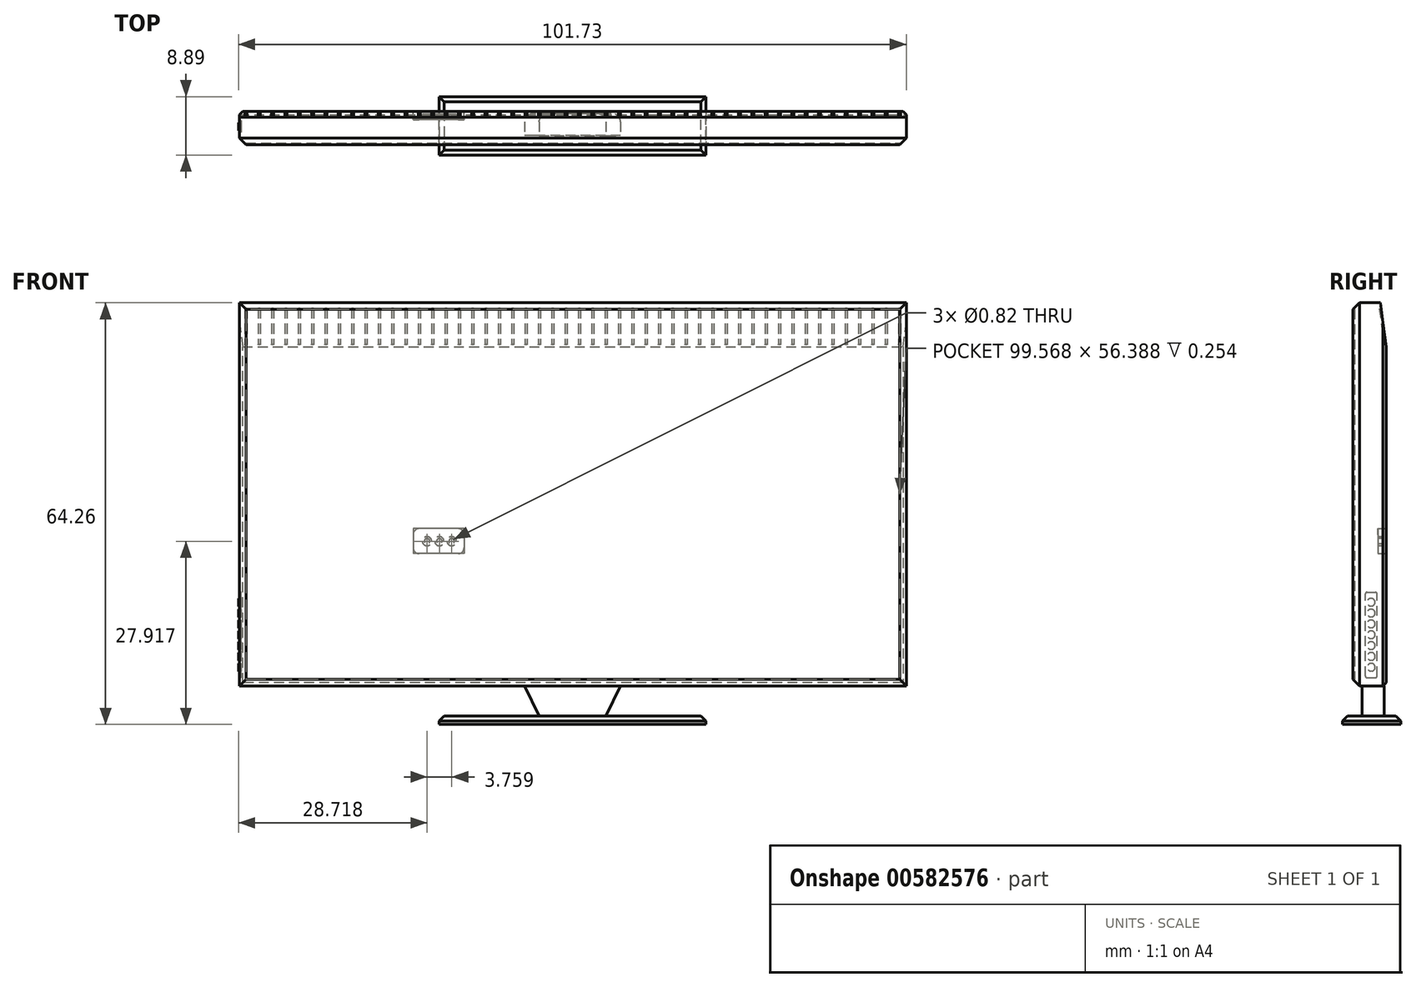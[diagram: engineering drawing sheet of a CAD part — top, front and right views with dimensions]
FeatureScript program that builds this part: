
annotation { "Feature Type Name" : "Feature", "Feature Type Description" : "" }
export const myFeature = defineFeature(function(context is Context, id is Id, definition is map)
    precondition{}
    {
        {
            var Q0;
            Q0=qCreatedBy(makeId("Front.planeOp"),FACE);
            var sketch = newSketch(context, id + "F0", { "sketchPlane" : qUnion([Q0])});
            skLineSegment(sketch, "E0", {"start": v(-47.44, 48.24) * mm, "end": v(54.16, 48.24) * mm});
            skLineSegment(sketch, "E1", {"start": v(54.16, 48.24) * mm, "end": v(54.16, -10.18) * mm});
            skLineSegment(sketch, "E2", {"start": v(54.16, -10.18) * mm, "end": v(-47.44, -10.18) * mm});
            skLineSegment(sketch, "E3", {"start": v(-47.44, -10.18) * mm, "end": v(-47.44, 48.24) * mm});
            skLineSegment(sketch, "E4", {"start": v(3.33, -14.75) * mm, "end": v(8.41, -14.75) * mm});
            skLineSegment(sketch, "E5", {"start": v(8.41, -14.75) * mm, "end": v(10.63, -10.18) * mm});
            skLineSegment(sketch, "E6", {"start": v(3.33, -14.75) * mm, "end": v(-1.75, -14.75) * mm});
            skLineSegment(sketch, "E7", {"start": v(-1.75, -14.75) * mm, "end": v(-3.97, -10.18) * mm});
            skSolve(sketch);
        }
        {
            var Q0;
            Q0=makeQuery(id+"F0.imprint","IMPRINT",FACE,{"disambiguationData":[TD([[makeQuery(id+"F0.imprint","IMPRINT",EDGE,{"derivedFrom":sQuery(id+"F0.wireOp",EDGE,"E0")}),-1.0]])]});
            extrude(context, id + "F1", {"entities" : qUnion([Q0]), "oppositeDirection" : true, "depth" : 5.08 * mm, "offsetDistance" : 25.4 * mm});
        }
        {
            var Q0;
            Q0=makeQuery(id+"F1.opExtrude","CAP_FACE",FACE,{"disambiguationData":[OSD([sQuery(id+"F0.wireOp",EDGE,"E0"),sQuery(id+"F0.wireOp",EDGE,"E1"),sQuery(id+"F0.wireOp",EDGE,"E2"),sQuery(id+"F0.wireOp",EDGE,"E3")])],"isStart":true});
            var sketch = newSketch(context, id + "F2", { "sketchPlane" : qUnion([Q0])});
            skLineSegment(sketch, "E8", {"start": v(-45.63, 49.46) * mm, "end": v(52.17, 49.46) * mm});
            skLineSegment(sketch, "E9", {"start": v(52.17, 49.46) * mm, "end": v(52.17, -7.5) * mm});
            skLineSegment(sketch, "E10", {"start": v(52.17, -7.5) * mm, "end": v(-45.41, -7.5) * mm});
            skLineSegment(sketch, "E11", {"start": v(-45.41, -7.5) * mm, "end": v(-45.63, 49.46) * mm});
            skSolve(sketch);
        }
        {
            var Q0;
            Q0=makeQuery(id+"F2.imprint","IMPRINT",FACE,{"disambiguationData":[TD([[makeQuery(id+"F2.imprint","IMPRINT",EDGE,{"derivedFrom":sQuery(id+"F2.wireOp",EDGE,"E8")}),-1.0]])]});
            extrude(context, id + "F3", {"entities" : qUnion([Q0]), "operationType" : NewBodyOperationType.REMOVE, "oppositeDirection" : true, "depth" : 0.5 * mm, "offsetDistance" : 25.4 * mm});
        }
        {
            var Q0;
            Q0=makeQuery(id+"F1.opExtrude","CAP_EDGE",EDGE,{"disambiguationData":[OSD([sQuery(id+"F0.wireOp",EDGE,"E3")])],"isStart":true});
            chamfer(context, id + "F4", {"entities" : qUnion([Q0]), "width" : 1.02 * mm, "tangentPropagation" : true});
        }
        {
            var Q0;
            Q0=makeQuery(id+"F1.opExtrude","CAP_EDGE",EDGE,{"disambiguationData":[OSD([sQuery(id+"F0.wireOp",EDGE,"E0")])],"isStart":true});
            chamfer(context, id + "F5", {"entities" : qUnion([Q0]), "width" : 1.02 * mm, "tangentPropagation" : true});
        }
        {
            var Q0;
            Q0=makeQuery(id+"F1.opExtrude","CAP_EDGE",EDGE,{"disambiguationData":[OSD([sQuery(id+"F0.wireOp",EDGE,"E1")])],"isStart":true});
            chamfer(context, id + "F6", {"entities" : qUnion([Q0]), "width" : 1.02 * mm, "tangentPropagation" : true});
        }
        {
            var Q0;
            Q0=makeQuery(id+"F1.opExtrude","CAP_EDGE",EDGE,{"disambiguationData":[OSD([sQuery(id+"F0.wireOp",EDGE,"E2")])],"isStart":true});
            chamfer(context, id + "F7", {"entities" : qUnion([Q0]), "width" : 1.02 * mm, "tangentPropagation" : true});
        }
        {
            var Q0;
            Q0=makeQuery(id+"F1.opExtrude","SWEPT_FACE",FACE,{"disambiguationData":[OSD([sQuery(id+"F0.wireOp",EDGE,"E1")])]});
            var sketch = newSketch(context, id + "F8", { "sketchPlane" : qUnion([Q0])});
            skLineSegment(sketch, "E12", {"start": v(4.16, 48.24) * mm, "end": v(5.08, 41.52) * mm});
            skLineSegment(sketch, "E13", {"start": v(5.08, 41.52) * mm, "end": v(5.08, 48.24) * mm});
            skLineSegment(sketch, "E14", {"start": v(5.08, 48.24) * mm, "end": v(4.16, 48.24) * mm});
            skSolve(sketch);
        }
        {
            var Q0;
            Q0=makeQuery(id+"F8.imprint","IMPRINT",FACE,{"disambiguationData":[TD([[makeQuery(id+"F8.imprint","IMPRINT",EDGE,{"derivedFrom":sQuery(id+"F8.wireOp",EDGE,"E12")}),1.0]])]});
            var Q1;
            Q1=makeQuery(id+"F1.opExtrude","SWEPT_FACE",FACE,{"disambiguationData":[OSD([sQuery(id+"F0.wireOp",EDGE,"E3")])]});
            extrude(context, id + "F9", {"entities" : qUnion([Q0]), "operationType" : NewBodyOperationType.REMOVE, "endBound" : BoundingType.UP_TO_SURFACE, "oppositeDirection" : true, "depth" : 25.4 * mm, "endBoundEntityFace" : qUnion([Q1]), "offsetDistance" : 25.4 * mm});
        }
        {
            var Q0;
            Q0=makeQuery(id+"F0.imprint","IMPRINT",FACE,{"disambiguationData":[TD([[makeQuery(id+"F0.imprint","IMPRINT",EDGE,{"derivedFrom":sQuery(id+"F0.wireOp",EDGE,"E4")}),1.0]])]});
            extrude(context, id + "F10", {"entities" : qUnion([Q0]), "oppositeDirection" : true, "depth" : 4.75 * mm, "offsetDistance" : 25.4 * mm});
        }
        {
            var Q0;
            Q0=makeQuery(id+"F10.opExtrude","CAP_FACE",FACE,{"disambiguationData":[OSD([sQuery(id+"F0.wireOp",EDGE,"E2"),sQuery(id+"F0.wireOp",EDGE,"E4"),sQuery(id+"F0.wireOp",EDGE,"E5"),sQuery(id+"F0.wireOp",EDGE,"E6"),sQuery(id+"F0.wireOp",EDGE,"E7")])],"isStart":true});
            extrude(context, id + "F11", {"entities" : qUnion([Q0]), "operationType" : NewBodyOperationType.REMOVE, "oppositeDirection" : true, "depth" : 1.4 * mm, "offsetDistance" : 25.4 * mm});
        }
        {
            var Q0;
            Q0=makeQuery(id+"F10.opExtrude","SWEPT_FACE",FACE,{"disambiguationData":[OSD([sQuery(id+"F0.wireOp",EDGE,"E4"),sQuery(id+"F0.wireOp",EDGE,"E6")])]});
            var sketch = newSketch(context, id + "F12", { "sketchPlane" : qUnion([Q0])});
            skLineSegment(sketch, "E15", {"start": v(3.33, -3.07) * mm, "end": v(3.33, 1.6) * mm});
            skPoint(sketch, "E15.startSnap0", {"position": v(3.33, -1.4) * mm});
            skPoint(sketch, "E15.startSnap1", {"position": v(-1.75, -3.07) * mm});
            skLineSegment(sketch, "E16", {"start": v(3.33, 1.6) * mm, "end": v(3.33, -3.07) * mm});
            skLineSegment(sketch, "E17", {"start": v(3.33, -7.3) * mm, "end": v(3.33, -3.07) * mm});
            skLineSegment(sketch, "E18", {"start": v(-16.99, 1.6) * mm, "end": v(23.65, 1.6) * mm});
            skLineSegment(sketch, "E19", {"start": v(23.65, 1.6) * mm, "end": v(23.65, -7.3) * mm});
            skLineSegment(sketch, "E20", {"start": v(23.65, -7.3) * mm, "end": v(-16.99, -7.3) * mm});
            skLineSegment(sketch, "E21", {"start": v(-16.99, -7.3) * mm, "end": v(-16.99, 1.6) * mm});
            skSolve(sketch);
        }
        {
            var Q0;
            {var subQ3=sQuery(id+"F12.wireOp",EDGE,"E21");Q0=makeQuery(id+"F12.imprint","IMPRINT",FACE,{"disambiguationData":[TD([[makeQuery(id+"F12.imprint","IMPRINT",EDGE,{"derivedFrom":subQ3}),-1.0]])]});}
            var Q1;
            {var subQ0=sQuery(id+"F12.wireOp",EDGE,"E19");Q1=makeQuery(id+"F12.imprint","IMPRINT",FACE,{"disambiguationData":[TD([[makeQuery(id+"F12.imprint","IMPRINT",EDGE,{"derivedFrom":subQ0}),-1.0]])]});}
            var Q2;
            {var subQ0=sQuery(id+"F0.wireOp",EDGE,"E4");var subQ1=makeQuery(id+"F10.opExtrude","SWEPT_EDGE",EDGE,{"disambiguationData":[OSD([subQ0,sQuery(id+"F0.wireOp",EDGE,"E5")])]});Q2=makeQuery(id+"F12.imprint","IMPRINT",FACE,{"disambiguationData":[TD([[makeQuery(id+"F12.imprint","IMPRINT",EDGE,{"derivedFrom":subQ1}),1.0]])]});}
            var Q3;
            {var subQ0=sQuery(id+"F0.wireOp",EDGE,"E6");var subQ1=makeQuery(id+"F10.opExtrude","SWEPT_EDGE",EDGE,{"disambiguationData":[OSD([subQ0,sQuery(id+"F0.wireOp",EDGE,"E7")])]});Q3=makeQuery(id+"F12.imprint","IMPRINT",FACE,{"disambiguationData":[TD([[makeQuery(id+"F12.imprint","IMPRINT",EDGE,{"derivedFrom":subQ1}),-1.0]])]});}
            extrude(context, id + "F13", {"entities" : qUnion([Q0, Q1, Q2, Q3]), "operationType" : NewBodyOperationType.ADD, "depth" : 1.27 * mm, "offsetDistance" : 25.4 * mm});
        }
        {
            var Q0;
            Q0=makeQuery(id+"F10.opExtrude","CAP_EDGE",EDGE,{"disambiguationData":[OSD([sQuery(id+"F0.wireOp",EDGE,"E7")])],"isStart":false});
            var Q1;
            Q1=makeQuery(id+"F11.boolean.opBoolean","COPY",EDGE,{"derivedFrom":makeQuery(id+"F11.opExtrude","CAP_EDGE",EDGE,{"disambiguationData":[OSD([sQuery(id+"F0.wireOp",EDGE,"E7")])],"isStart":false})});
            var Q2;
            Q2=makeQuery(id+"F11.boolean.opBoolean","COPY",EDGE,{"derivedFrom":makeQuery(id+"F11.opExtrude","CAP_EDGE",EDGE,{"disambiguationData":[OSD([sQuery(id+"F0.wireOp",EDGE,"E5")])],"isStart":false})});
            var Q3;
            Q3=makeQuery(id+"F10.opExtrude","CAP_EDGE",EDGE,{"disambiguationData":[OSD([sQuery(id+"F0.wireOp",EDGE,"E5")])],"isStart":false});
            fillet(context, id + "F14", {"entities" : qUnion([Q0, Q1, Q2, Q3]), "radius" : 1.27 * mm, "tangentPropagation" : true, "allowEdgeOverflow" : false});
        }
        {
            var Q0;
            Q0=makeQuery(id+"F13.opExtrude","CAP_EDGE",EDGE,{"disambiguationData":[OSD([sQuery(id+"F12.wireOp",EDGE,"E21")])],"isStart":true});
            var Q1;
            Q1=makeQuery(id+"F13.opExtrude","CAP_EDGE",EDGE,{"disambiguationData":[OSD([sQuery(id+"F12.wireOp",EDGE,"E18")])],"isStart":true});
            var Q2;
            Q2=makeQuery(id+"F13.opExtrude","CAP_EDGE",EDGE,{"disambiguationData":[OSD([sQuery(id+"F12.wireOp",EDGE,"E19")])],"isStart":true});
            var Q3;
            Q3=makeQuery(id+"F13.opExtrude","CAP_EDGE",EDGE,{"disambiguationData":[OSD([sQuery(id+"F12.wireOp",EDGE,"E20")])],"isStart":true});
            chamfer(context, id + "F15", {"entities" : qUnion([Q0, Q1, Q2, Q3]), "width" : 0.76 * mm, "tangentPropagation" : true});
        }
        {
            var Q0;
            Q0=makeQuery(id+"F1.opExtrude","CAP_EDGE",EDGE,{"disambiguationData":[OSD([sQuery(id+"F0.wireOp",EDGE,"E3")])],"isStart":false});
            var Q1;
            Q1=makeQuery(id+"F1.opExtrude","CAP_EDGE",EDGE,{"disambiguationData":[OSD([sQuery(id+"F0.wireOp",EDGE,"E1")])],"isStart":false});
            var Q2;
            Q2=makeQuery(id+"F1.opExtrude","CAP_EDGE",EDGE,{"disambiguationData":[OSD([sQuery(id+"F0.wireOp",EDGE,"E2")])],"isStart":false});
            var Q3;
            Q3=makeQuery(id+"F9.boolean.opBoolean","COPY",EDGE,{"derivedFrom":makeQuery(id+"F9.opExtrude","SWEPT_EDGE",EDGE,{"disambiguationData":[OSD([sQuery(id+"F0.wireOp",EDGE,"E0"),sQuery(id+"F0.wireOp",EDGE,"E1"),sQuery(id+"F8.wireOp",EDGE,"E12"),sQuery(id+"F8.wireOp",EDGE,"E14")])]})});
            chamfer(context, id + "F16", {"entities" : qUnion([Q0, Q1, Q2, Q3]), "width" : 0.5 * mm, "tangentPropagation" : true});
        }
        {
            var Q0;
            Q0=makeQuery(id+"F1.opExtrude","CAP_FACE",FACE,{"disambiguationData":[OSD([sQuery(id+"F0.wireOp",EDGE,"E0"),sQuery(id+"F0.wireOp",EDGE,"E1"),sQuery(id+"F0.wireOp",EDGE,"E2"),sQuery(id+"F0.wireOp",EDGE,"E3")])],"isStart":true});
            extrude(context, id + "F17", {"entities" : qUnion([Q0]), "operationType" : NewBodyOperationType.REMOVE, "oppositeDirection" : true, "depth" : 0.25 * mm, "offsetDistance" : 25.4 * mm});
        }
        {
            var Q0;
            Q0=makeQuery(id+"F17.boolean.opBoolean","COPY",FACE,{"derivedFrom":makeQuery(id+"F17.opExtrude","CAP_FACE",FACE,{"disambiguationData":[OSD([sQuery(id+"F0.wireOp",EDGE,"E0"),sQuery(id+"F0.wireOp",EDGE,"E1"),sQuery(id+"F0.wireOp",EDGE,"E2"),sQuery(id+"F0.wireOp",EDGE,"E3")])],"isStart":false})});
            extrude(context, id + "F18", {"entities" : qUnion([Q0]), "depth" : 0.03 * mm, "offsetDistance" : 25.4 * mm});
        }
        {
            var Q0;
            Q0=makeQuery(id+"F9.boolean.opBoolean","COPY",FACE,{"derivedFrom":makeQuery(id+"F9.opExtrude","SWEPT_FACE",FACE,{"disambiguationData":[OSD([sQuery(id+"F8.wireOp",EDGE,"E12")])]})});
            var sketch = newSketch(context, id + "F19", { "sketchPlane" : qUnion([Q0])});
            skLineSegment(sketch, "E22.bottom", {"start": v(-53.3, 46.33) * mm, "end": v(-53, 46.33) * mm});
            skLineSegment(sketch, "E22.top", {"start": v(-53.3, 40.82) * mm, "end": v(-53, 40.82) * mm});
            skLineSegment(sketch, "E22.left", {"start": v(-53.3, 46.33) * mm, "end": v(-53.3, 40.82) * mm});
            skLineSegment(sketch, "E22.right", {"start": v(-53, 46.33) * mm, "end": v(-53, 40.82) * mm});
            skLineSegment(sketch, "E23.1.0.0", {"start": v(-51.28, 46.33) * mm, "end": v(-51.28, 40.82) * mm});
            skLineSegment(sketch, "E23.1.0.1", {"start": v(-50.96, 46.33) * mm, "end": v(-50.96, 40.82) * mm});
            skLineSegment(sketch, "E23.1.0.2", {"start": v(-51.28, 40.82) * mm, "end": v(-50.96, 40.82) * mm});
            skLineSegment(sketch, "E23.1.0.3", {"start": v(-51.28, 46.33) * mm, "end": v(-50.96, 46.33) * mm});
            skLineSegment(sketch, "E23.2.0.0", {"start": v(-49.24, 46.33) * mm, "end": v(-49.24, 40.82) * mm});
            skLineSegment(sketch, "E23.2.0.1", {"start": v(-48.93, 46.33) * mm, "end": v(-48.93, 40.82) * mm});
            skLineSegment(sketch, "E23.2.0.2", {"start": v(-49.24, 40.82) * mm, "end": v(-48.93, 40.82) * mm});
            skLineSegment(sketch, "E23.2.0.3", {"start": v(-49.24, 46.33) * mm, "end": v(-48.93, 46.33) * mm});
            skLineSegment(sketch, "E23.3.0.0", {"start": v(-47.21, 46.33) * mm, "end": v(-47.21, 40.82) * mm});
            skLineSegment(sketch, "E23.3.0.1", {"start": v(-46.9, 46.33) * mm, "end": v(-46.9, 40.82) * mm});
            skLineSegment(sketch, "E23.3.0.2", {"start": v(-47.21, 40.82) * mm, "end": v(-46.9, 40.82) * mm});
            skLineSegment(sketch, "E23.3.0.3", {"start": v(-47.21, 46.33) * mm, "end": v(-46.9, 46.33) * mm});
            skLineSegment(sketch, "E23.4.0.0", {"start": v(-45.18, 46.33) * mm, "end": v(-45.18, 40.82) * mm});
            skLineSegment(sketch, "E23.4.0.1", {"start": v(-44.86, 46.33) * mm, "end": v(-44.86, 40.82) * mm});
            skLineSegment(sketch, "E23.4.0.2", {"start": v(-45.18, 40.82) * mm, "end": v(-44.86, 40.82) * mm});
            skLineSegment(sketch, "E23.4.0.3", {"start": v(-45.18, 46.33) * mm, "end": v(-44.86, 46.33) * mm});
            skLineSegment(sketch, "E23.5.0.0", {"start": v(-43.15, 46.33) * mm, "end": v(-43.15, 40.82) * mm});
            skLineSegment(sketch, "E23.5.0.1", {"start": v(-42.83, 46.33) * mm, "end": v(-42.83, 40.82) * mm});
            skLineSegment(sketch, "E23.5.0.2", {"start": v(-43.15, 40.82) * mm, "end": v(-42.83, 40.82) * mm});
            skLineSegment(sketch, "E23.5.0.3", {"start": v(-43.15, 46.33) * mm, "end": v(-42.83, 46.33) * mm});
            skLineSegment(sketch, "E23.6.0.0", {"start": v(-41.12, 46.33) * mm, "end": v(-41.12, 40.82) * mm});
            skLineSegment(sketch, "E23.6.0.1", {"start": v(-40.8, 46.33) * mm, "end": v(-40.8, 40.82) * mm});
            skLineSegment(sketch, "E23.6.0.2", {"start": v(-41.12, 40.82) * mm, "end": v(-40.8, 40.82) * mm});
            skLineSegment(sketch, "E23.6.0.3", {"start": v(-41.12, 46.33) * mm, "end": v(-40.8, 46.33) * mm});
            skLineSegment(sketch, "E23.7.0.0", {"start": v(-39.08, 46.33) * mm, "end": v(-39.08, 40.82) * mm});
            skLineSegment(sketch, "E23.7.0.1", {"start": v(-38.77, 46.33) * mm, "end": v(-38.77, 40.82) * mm});
            skLineSegment(sketch, "E23.7.0.2", {"start": v(-39.08, 40.82) * mm, "end": v(-38.77, 40.82) * mm});
            skLineSegment(sketch, "E23.7.0.3", {"start": v(-39.08, 46.33) * mm, "end": v(-38.77, 46.33) * mm});
            skLineSegment(sketch, "E23.8.0.0", {"start": v(-37.05, 46.33) * mm, "end": v(-37.05, 40.82) * mm});
            skLineSegment(sketch, "E23.8.0.1", {"start": v(-36.74, 46.33) * mm, "end": v(-36.74, 40.82) * mm});
            skLineSegment(sketch, "E23.8.0.2", {"start": v(-37.05, 40.82) * mm, "end": v(-36.74, 40.82) * mm});
            skLineSegment(sketch, "E23.8.0.3", {"start": v(-37.05, 46.33) * mm, "end": v(-36.74, 46.33) * mm});
            skLineSegment(sketch, "E23.9.0.0", {"start": v(-35.02, 46.33) * mm, "end": v(-35.02, 40.82) * mm});
            skLineSegment(sketch, "E23.9.0.1", {"start": v(-34.7, 46.33) * mm, "end": v(-34.7, 40.82) * mm});
            skLineSegment(sketch, "E23.9.0.2", {"start": v(-35.02, 40.82) * mm, "end": v(-34.7, 40.82) * mm});
            skLineSegment(sketch, "E23.9.0.3", {"start": v(-35.02, 46.33) * mm, "end": v(-34.7, 46.33) * mm});
            skLineSegment(sketch, "E23.10.0.0", {"start": v(-32.99, 46.33) * mm, "end": v(-32.99, 40.82) * mm});
            skLineSegment(sketch, "E23.10.0.1", {"start": v(-32.67, 46.33) * mm, "end": v(-32.67, 40.82) * mm});
            skLineSegment(sketch, "E23.10.0.2", {"start": v(-32.99, 40.82) * mm, "end": v(-32.67, 40.82) * mm});
            skLineSegment(sketch, "E23.10.0.3", {"start": v(-32.99, 46.33) * mm, "end": v(-32.67, 46.33) * mm});
            skLineSegment(sketch, "E23.11.0.0", {"start": v(-30.96, 46.33) * mm, "end": v(-30.96, 40.82) * mm});
            skLineSegment(sketch, "E23.11.0.1", {"start": v(-30.64, 46.33) * mm, "end": v(-30.64, 40.82) * mm});
            skLineSegment(sketch, "E23.11.0.2", {"start": v(-30.96, 40.82) * mm, "end": v(-30.64, 40.82) * mm});
            skLineSegment(sketch, "E23.11.0.3", {"start": v(-30.96, 46.33) * mm, "end": v(-30.64, 46.33) * mm});
            skLineSegment(sketch, "E23.12.0.0", {"start": v(-28.92, 46.33) * mm, "end": v(-28.92, 40.82) * mm});
            skLineSegment(sketch, "E23.12.0.1", {"start": v(-28.6, 46.33) * mm, "end": v(-28.6, 40.82) * mm});
            skLineSegment(sketch, "E23.12.0.2", {"start": v(-28.92, 40.82) * mm, "end": v(-28.6, 40.82) * mm});
            skLineSegment(sketch, "E23.12.0.3", {"start": v(-28.92, 46.33) * mm, "end": v(-28.6, 46.33) * mm});
            skLineSegment(sketch, "E23.13.0.0", {"start": v(-26.9, 46.33) * mm, "end": v(-26.9, 40.82) * mm});
            skLineSegment(sketch, "E23.13.0.1", {"start": v(-26.58, 46.33) * mm, "end": v(-26.58, 40.82) * mm});
            skLineSegment(sketch, "E23.13.0.2", {"start": v(-26.9, 40.82) * mm, "end": v(-26.58, 40.82) * mm});
            skLineSegment(sketch, "E23.13.0.3", {"start": v(-26.9, 46.33) * mm, "end": v(-26.58, 46.33) * mm});
            skLineSegment(sketch, "E23.14.0.0", {"start": v(-24.86, 46.33) * mm, "end": v(-24.86, 40.82) * mm});
            skLineSegment(sketch, "E23.14.0.1", {"start": v(-24.54, 46.33) * mm, "end": v(-24.54, 40.82) * mm});
            skLineSegment(sketch, "E23.14.0.2", {"start": v(-24.86, 40.82) * mm, "end": v(-24.54, 40.82) * mm});
            skLineSegment(sketch, "E23.14.0.3", {"start": v(-24.86, 46.33) * mm, "end": v(-24.54, 46.33) * mm});
            skLineSegment(sketch, "E23.15.0.0", {"start": v(-22.83, 46.33) * mm, "end": v(-22.83, 40.82) * mm});
            skLineSegment(sketch, "E23.15.0.1", {"start": v(-22.51, 46.33) * mm, "end": v(-22.51, 40.82) * mm});
            skLineSegment(sketch, "E23.15.0.2", {"start": v(-22.83, 40.82) * mm, "end": v(-22.51, 40.82) * mm});
            skLineSegment(sketch, "E23.15.0.3", {"start": v(-22.83, 46.33) * mm, "end": v(-22.51, 46.33) * mm});
            skLineSegment(sketch, "E23.16.0.0", {"start": v(-20.8, 46.33) * mm, "end": v(-20.8, 40.82) * mm});
            skLineSegment(sketch, "E23.16.0.1", {"start": v(-20.48, 46.33) * mm, "end": v(-20.48, 40.82) * mm});
            skLineSegment(sketch, "E23.16.0.2", {"start": v(-20.8, 40.82) * mm, "end": v(-20.48, 40.82) * mm});
            skLineSegment(sketch, "E23.16.0.3", {"start": v(-20.8, 46.33) * mm, "end": v(-20.48, 46.33) * mm});
            skLineSegment(sketch, "E23.17.0.0", {"start": v(-18.76, 46.33) * mm, "end": v(-18.76, 40.82) * mm});
            skLineSegment(sketch, "E23.17.0.1", {"start": v(-18.45, 46.33) * mm, "end": v(-18.45, 40.82) * mm});
            skLineSegment(sketch, "E23.17.0.2", {"start": v(-18.76, 40.82) * mm, "end": v(-18.45, 40.82) * mm});
            skLineSegment(sketch, "E23.17.0.3", {"start": v(-18.76, 46.33) * mm, "end": v(-18.45, 46.33) * mm});
            skLineSegment(sketch, "E23.18.0.0", {"start": v(-16.73, 46.33) * mm, "end": v(-16.73, 40.82) * mm});
            skLineSegment(sketch, "E23.18.0.1", {"start": v(-16.42, 46.33) * mm, "end": v(-16.42, 40.82) * mm});
            skLineSegment(sketch, "E23.18.0.2", {"start": v(-16.73, 40.82) * mm, "end": v(-16.42, 40.82) * mm});
            skLineSegment(sketch, "E23.18.0.3", {"start": v(-16.73, 46.33) * mm, "end": v(-16.42, 46.33) * mm});
            skLineSegment(sketch, "E23.19.0.0", {"start": v(-14.7, 46.33) * mm, "end": v(-14.7, 40.82) * mm});
            skLineSegment(sketch, "E23.19.0.1", {"start": v(-14.38, 46.33) * mm, "end": v(-14.38, 40.82) * mm});
            skLineSegment(sketch, "E23.19.0.2", {"start": v(-14.7, 40.82) * mm, "end": v(-14.38, 40.82) * mm});
            skLineSegment(sketch, "E23.19.0.3", {"start": v(-14.7, 46.33) * mm, "end": v(-14.38, 46.33) * mm});
            skLineSegment(sketch, "E23.20.0.0", {"start": v(-12.67, 46.33) * mm, "end": v(-12.67, 40.82) * mm});
            skLineSegment(sketch, "E23.20.0.1", {"start": v(-12.35, 46.33) * mm, "end": v(-12.35, 40.82) * mm});
            skLineSegment(sketch, "E23.20.0.2", {"start": v(-12.67, 40.82) * mm, "end": v(-12.35, 40.82) * mm});
            skLineSegment(sketch, "E23.20.0.3", {"start": v(-12.67, 46.33) * mm, "end": v(-12.35, 46.33) * mm});
            skLineSegment(sketch, "E23.21.0.0", {"start": v(-10.64, 46.33) * mm, "end": v(-10.64, 40.82) * mm});
            skLineSegment(sketch, "E23.21.0.1", {"start": v(-10.32, 46.33) * mm, "end": v(-10.32, 40.82) * mm});
            skLineSegment(sketch, "E23.21.0.2", {"start": v(-10.64, 40.82) * mm, "end": v(-10.32, 40.82) * mm});
            skLineSegment(sketch, "E23.21.0.3", {"start": v(-10.64, 46.33) * mm, "end": v(-10.32, 46.33) * mm});
            skLineSegment(sketch, "E23.22.0.0", {"start": v(-8.6, 46.33) * mm, "end": v(-8.6, 40.82) * mm});
            skLineSegment(sketch, "E23.22.0.1", {"start": v(-8.29, 46.33) * mm, "end": v(-8.29, 40.82) * mm});
            skLineSegment(sketch, "E23.22.0.2", {"start": v(-8.6, 40.82) * mm, "end": v(-8.29, 40.82) * mm});
            skLineSegment(sketch, "E23.22.0.3", {"start": v(-8.6, 46.33) * mm, "end": v(-8.29, 46.33) * mm});
            skLineSegment(sketch, "E23.23.0.0", {"start": v(-6.57, 46.33) * mm, "end": v(-6.57, 40.82) * mm});
            skLineSegment(sketch, "E23.23.0.1", {"start": v(-6.26, 46.33) * mm, "end": v(-6.26, 40.82) * mm});
            skLineSegment(sketch, "E23.23.0.2", {"start": v(-6.57, 40.82) * mm, "end": v(-6.26, 40.82) * mm});
            skLineSegment(sketch, "E23.23.0.3", {"start": v(-6.57, 46.33) * mm, "end": v(-6.26, 46.33) * mm});
            skLineSegment(sketch, "E23.24.0.0", {"start": v(-4.54, 46.33) * mm, "end": v(-4.54, 40.82) * mm});
            skLineSegment(sketch, "E23.24.0.1", {"start": v(-4.22, 46.33) * mm, "end": v(-4.22, 40.82) * mm});
            skLineSegment(sketch, "E23.24.0.2", {"start": v(-4.54, 40.82) * mm, "end": v(-4.22, 40.82) * mm});
            skLineSegment(sketch, "E23.24.0.3", {"start": v(-4.54, 46.33) * mm, "end": v(-4.22, 46.33) * mm});
            skLineSegment(sketch, "E23.25.0.0", {"start": v(-2.5, 46.33) * mm, "end": v(-2.5, 40.82) * mm});
            skLineSegment(sketch, "E23.25.0.1", {"start": v(-2.2, 46.33) * mm, "end": v(-2.2, 40.82) * mm});
            skLineSegment(sketch, "E23.25.0.2", {"start": v(-2.5, 40.82) * mm, "end": v(-2.2, 40.82) * mm});
            skLineSegment(sketch, "E23.25.0.3", {"start": v(-2.5, 46.33) * mm, "end": v(-2.2, 46.33) * mm});
            skLineSegment(sketch, "E23.26.0.0", {"start": v(-0.48, 46.33) * mm, "end": v(-0.48, 40.82) * mm});
            skLineSegment(sketch, "E23.26.0.1", {"start": v(-0.16, 46.33) * mm, "end": v(-0.16, 40.82) * mm});
            skLineSegment(sketch, "E23.26.0.2", {"start": v(-0.48, 40.82) * mm, "end": v(-0.16, 40.82) * mm});
            skLineSegment(sketch, "E23.26.0.3", {"start": v(-0.48, 46.33) * mm, "end": v(-0.16, 46.33) * mm});
            skLineSegment(sketch, "E23.27.0.0", {"start": v(1.56, 46.33) * mm, "end": v(1.56, 40.82) * mm});
            skLineSegment(sketch, "E23.27.0.1", {"start": v(1.87, 46.33) * mm, "end": v(1.87, 40.82) * mm});
            skLineSegment(sketch, "E23.27.0.2", {"start": v(1.56, 40.82) * mm, "end": v(1.87, 40.82) * mm});
            skLineSegment(sketch, "E23.27.0.3", {"start": v(1.56, 46.33) * mm, "end": v(1.87, 46.33) * mm});
            skLineSegment(sketch, "E23.28.0.0", {"start": v(3.59, 46.33) * mm, "end": v(3.59, 40.82) * mm});
            skLineSegment(sketch, "E23.28.0.1", {"start": v(3.9, 46.33) * mm, "end": v(3.9, 40.82) * mm});
            skLineSegment(sketch, "E23.28.0.2", {"start": v(3.59, 40.82) * mm, "end": v(3.9, 40.82) * mm});
            skLineSegment(sketch, "E23.28.0.3", {"start": v(3.59, 46.33) * mm, "end": v(3.9, 46.33) * mm});
            skLineSegment(sketch, "E23.29.0.0", {"start": v(5.62, 46.33) * mm, "end": v(5.62, 40.82) * mm});
            skLineSegment(sketch, "E23.29.0.1", {"start": v(5.94, 46.33) * mm, "end": v(5.94, 40.82) * mm});
            skLineSegment(sketch, "E23.29.0.2", {"start": v(5.62, 40.82) * mm, "end": v(5.94, 40.82) * mm});
            skLineSegment(sketch, "E23.29.0.3", {"start": v(5.62, 46.33) * mm, "end": v(5.94, 46.33) * mm});
            skLineSegment(sketch, "E23.30.0.0", {"start": v(7.65, 46.33) * mm, "end": v(7.65, 40.82) * mm});
            skLineSegment(sketch, "E23.30.0.1", {"start": v(7.97, 46.33) * mm, "end": v(7.97, 40.82) * mm});
            skLineSegment(sketch, "E23.30.0.2", {"start": v(7.65, 40.82) * mm, "end": v(7.97, 40.82) * mm});
            skLineSegment(sketch, "E23.30.0.3", {"start": v(7.65, 46.33) * mm, "end": v(7.97, 46.33) * mm});
            skLineSegment(sketch, "E23.31.0.0", {"start": v(9.68, 46.33) * mm, "end": v(9.68, 40.82) * mm});
            skLineSegment(sketch, "E23.31.0.1", {"start": v(10, 46.33) * mm, "end": v(10, 40.82) * mm});
            skLineSegment(sketch, "E23.31.0.2", {"start": v(9.68, 40.82) * mm, "end": v(10, 40.82) * mm});
            skLineSegment(sketch, "E23.31.0.3", {"start": v(9.68, 46.33) * mm, "end": v(10, 46.33) * mm});
            skLineSegment(sketch, "E23.32.0.0", {"start": v(11.72, 46.33) * mm, "end": v(11.72, 40.82) * mm});
            skLineSegment(sketch, "E23.32.0.1", {"start": v(12.03, 46.33) * mm, "end": v(12.03, 40.82) * mm});
            skLineSegment(sketch, "E23.32.0.2", {"start": v(11.72, 40.82) * mm, "end": v(12.03, 40.82) * mm});
            skLineSegment(sketch, "E23.32.0.3", {"start": v(11.72, 46.33) * mm, "end": v(12.03, 46.33) * mm});
            skLineSegment(sketch, "E23.33.0.0", {"start": v(13.75, 46.33) * mm, "end": v(13.75, 40.82) * mm});
            skLineSegment(sketch, "E23.33.0.1", {"start": v(14.06, 46.33) * mm, "end": v(14.06, 40.82) * mm});
            skLineSegment(sketch, "E23.33.0.2", {"start": v(13.75, 40.82) * mm, "end": v(14.06, 40.82) * mm});
            skLineSegment(sketch, "E23.33.0.3", {"start": v(13.75, 46.33) * mm, "end": v(14.06, 46.33) * mm});
            skLineSegment(sketch, "E23.34.0.0", {"start": v(15.78, 46.33) * mm, "end": v(15.78, 40.82) * mm});
            skLineSegment(sketch, "E23.34.0.1", {"start": v(16.1, 46.33) * mm, "end": v(16.1, 40.82) * mm});
            skLineSegment(sketch, "E23.34.0.2", {"start": v(15.78, 40.82) * mm, "end": v(16.1, 40.82) * mm});
            skLineSegment(sketch, "E23.34.0.3", {"start": v(15.78, 46.33) * mm, "end": v(16.1, 46.33) * mm});
            skLineSegment(sketch, "E23.35.0.0", {"start": v(17.81, 46.33) * mm, "end": v(17.81, 40.82) * mm});
            skLineSegment(sketch, "E23.35.0.1", {"start": v(18.13, 46.33) * mm, "end": v(18.13, 40.82) * mm});
            skLineSegment(sketch, "E23.35.0.2", {"start": v(17.81, 40.82) * mm, "end": v(18.13, 40.82) * mm});
            skLineSegment(sketch, "E23.35.0.3", {"start": v(17.81, 46.33) * mm, "end": v(18.13, 46.33) * mm});
            skLineSegment(sketch, "E23.36.0.0", {"start": v(19.84, 46.33) * mm, "end": v(19.84, 40.82) * mm});
            skLineSegment(sketch, "E23.36.0.1", {"start": v(20.16, 46.33) * mm, "end": v(20.16, 40.82) * mm});
            skLineSegment(sketch, "E23.36.0.2", {"start": v(19.84, 40.82) * mm, "end": v(20.16, 40.82) * mm});
            skLineSegment(sketch, "E23.36.0.3", {"start": v(19.84, 46.33) * mm, "end": v(20.16, 46.33) * mm});
            skLineSegment(sketch, "E23.37.0.0", {"start": v(21.88, 46.33) * mm, "end": v(21.88, 40.82) * mm});
            skLineSegment(sketch, "E23.37.0.1", {"start": v(22.2, 46.33) * mm, "end": v(22.2, 40.82) * mm});
            skLineSegment(sketch, "E23.37.0.2", {"start": v(21.88, 40.82) * mm, "end": v(22.2, 40.82) * mm});
            skLineSegment(sketch, "E23.37.0.3", {"start": v(21.88, 46.33) * mm, "end": v(22.2, 46.33) * mm});
            skLineSegment(sketch, "E23.38.0.0", {"start": v(23.9, 46.33) * mm, "end": v(23.9, 40.82) * mm});
            skLineSegment(sketch, "E23.38.0.1", {"start": v(24.22, 46.33) * mm, "end": v(24.22, 40.82) * mm});
            skLineSegment(sketch, "E23.38.0.2", {"start": v(23.9, 40.82) * mm, "end": v(24.22, 40.82) * mm});
            skLineSegment(sketch, "E23.38.0.3", {"start": v(23.9, 46.33) * mm, "end": v(24.22, 46.33) * mm});
            skLineSegment(sketch, "E23.39.0.0", {"start": v(25.94, 46.33) * mm, "end": v(25.94, 40.82) * mm});
            skLineSegment(sketch, "E23.39.0.1", {"start": v(26.26, 46.33) * mm, "end": v(26.26, 40.82) * mm});
            skLineSegment(sketch, "E23.39.0.2", {"start": v(25.94, 40.82) * mm, "end": v(26.26, 40.82) * mm});
            skLineSegment(sketch, "E23.39.0.3", {"start": v(25.94, 46.33) * mm, "end": v(26.26, 46.33) * mm});
            skLineSegment(sketch, "E23.40.0.0", {"start": v(27.97, 46.33) * mm, "end": v(27.97, 40.82) * mm});
            skLineSegment(sketch, "E23.40.0.1", {"start": v(28.29, 46.33) * mm, "end": v(28.29, 40.82) * mm});
            skLineSegment(sketch, "E23.40.0.2", {"start": v(27.97, 40.82) * mm, "end": v(28.29, 40.82) * mm});
            skLineSegment(sketch, "E23.40.0.3", {"start": v(27.97, 46.33) * mm, "end": v(28.29, 46.33) * mm});
            skLineSegment(sketch, "E23.41.0.0", {"start": v(30, 46.33) * mm, "end": v(30, 40.82) * mm});
            skLineSegment(sketch, "E23.41.0.1", {"start": v(30.32, 46.33) * mm, "end": v(30.32, 40.82) * mm});
            skLineSegment(sketch, "E23.41.0.2", {"start": v(30, 40.82) * mm, "end": v(30.32, 40.82) * mm});
            skLineSegment(sketch, "E23.41.0.3", {"start": v(30, 46.33) * mm, "end": v(30.32, 46.33) * mm});
            skLineSegment(sketch, "E23.42.0.0", {"start": v(32.04, 46.33) * mm, "end": v(32.04, 40.82) * mm});
            skLineSegment(sketch, "E23.42.0.1", {"start": v(32.35, 46.33) * mm, "end": v(32.35, 40.82) * mm});
            skLineSegment(sketch, "E23.42.0.2", {"start": v(32.04, 40.82) * mm, "end": v(32.35, 40.82) * mm});
            skLineSegment(sketch, "E23.42.0.3", {"start": v(32.04, 46.33) * mm, "end": v(32.35, 46.33) * mm});
            skLineSegment(sketch, "E23.43.0.0", {"start": v(34.07, 46.33) * mm, "end": v(34.07, 40.82) * mm});
            skLineSegment(sketch, "E23.43.0.1", {"start": v(34.38, 46.33) * mm, "end": v(34.38, 40.82) * mm});
            skLineSegment(sketch, "E23.43.0.2", {"start": v(34.07, 40.82) * mm, "end": v(34.38, 40.82) * mm});
            skLineSegment(sketch, "E23.43.0.3", {"start": v(34.07, 46.33) * mm, "end": v(34.38, 46.33) * mm});
            skLineSegment(sketch, "E23.44.0.0", {"start": v(36.1, 46.33) * mm, "end": v(36.1, 40.82) * mm});
            skLineSegment(sketch, "E23.44.0.1", {"start": v(36.42, 46.33) * mm, "end": v(36.42, 40.82) * mm});
            skLineSegment(sketch, "E23.44.0.2", {"start": v(36.1, 40.82) * mm, "end": v(36.42, 40.82) * mm});
            skLineSegment(sketch, "E23.44.0.3", {"start": v(36.1, 46.33) * mm, "end": v(36.42, 46.33) * mm});
            skLineSegment(sketch, "E23.45.0.0", {"start": v(38.13, 46.33) * mm, "end": v(38.13, 40.82) * mm});
            skLineSegment(sketch, "E23.45.0.1", {"start": v(38.45, 46.33) * mm, "end": v(38.45, 40.82) * mm});
            skLineSegment(sketch, "E23.45.0.2", {"start": v(38.13, 40.82) * mm, "end": v(38.45, 40.82) * mm});
            skLineSegment(sketch, "E23.45.0.3", {"start": v(38.13, 46.33) * mm, "end": v(38.45, 46.33) * mm});
            skLineSegment(sketch, "E23.46.0.0", {"start": v(40.16, 46.33) * mm, "end": v(40.16, 40.82) * mm});
            skLineSegment(sketch, "E23.46.0.1", {"start": v(40.48, 46.33) * mm, "end": v(40.48, 40.82) * mm});
            skLineSegment(sketch, "E23.46.0.2", {"start": v(40.16, 40.82) * mm, "end": v(40.48, 40.82) * mm});
            skLineSegment(sketch, "E23.46.0.3", {"start": v(40.16, 46.33) * mm, "end": v(40.48, 46.33) * mm});
            skLineSegment(sketch, "E23.47.0.0", {"start": v(42.2, 46.33) * mm, "end": v(42.2, 40.82) * mm});
            skLineSegment(sketch, "E23.47.0.1", {"start": v(42.51, 46.33) * mm, "end": v(42.51, 40.82) * mm});
            skLineSegment(sketch, "E23.47.0.2", {"start": v(42.2, 40.82) * mm, "end": v(42.51, 40.82) * mm});
            skLineSegment(sketch, "E23.47.0.3", {"start": v(42.2, 46.33) * mm, "end": v(42.51, 46.33) * mm});
            skLineSegment(sketch, "E23.48.0.0", {"start": v(44.23, 46.33) * mm, "end": v(44.23, 40.82) * mm});
            skLineSegment(sketch, "E23.48.0.1", {"start": v(44.54, 46.33) * mm, "end": v(44.54, 40.82) * mm});
            skLineSegment(sketch, "E23.48.0.2", {"start": v(44.23, 40.82) * mm, "end": v(44.54, 40.82) * mm});
            skLineSegment(sketch, "E23.48.0.3", {"start": v(44.23, 46.33) * mm, "end": v(44.54, 46.33) * mm});
            skLineSegment(sketch, "E23.49.0.0", {"start": v(46.26, 46.33) * mm, "end": v(46.26, 40.82) * mm});
            skLineSegment(sketch, "E23.49.0.1", {"start": v(46.58, 46.33) * mm, "end": v(46.58, 40.82) * mm});
            skLineSegment(sketch, "E23.49.0.2", {"start": v(46.26, 40.82) * mm, "end": v(46.58, 40.82) * mm});
            skLineSegment(sketch, "E23.49.0.3", {"start": v(46.26, 46.33) * mm, "end": v(46.58, 46.33) * mm});
            skLineSegment(sketch, "E23.direction1", {"start": v(-53.3, 40.82) * mm, "end": v(-51.28, 40.82) * mm, "construction": true});
            skSolve(sketch);
        }
        {
            var Q0;
            Q0=makeQuery(id+"F19.imprint","IMPRINT",FACE,{"disambiguationData":[TD([[makeQuery(id+"F19.imprint","IMPRINT",EDGE,{"derivedFrom":sQuery(id+"F19.wireOp",EDGE,"E22.bottom")}),-1.0]])]});
            var Q1;
            Q1=makeQuery(id+"F19.imprint","IMPRINT",FACE,{"disambiguationData":[TD([[makeQuery(id+"F19.imprint","IMPRINT",EDGE,{"derivedFrom":sQuery(id+"F19.wireOp",EDGE,"E23.1.0.0")}),1.0]])]});
            var Q2;
            Q2=makeQuery(id+"F19.imprint","IMPRINT",FACE,{"disambiguationData":[TD([[makeQuery(id+"F19.imprint","IMPRINT",EDGE,{"derivedFrom":sQuery(id+"F19.wireOp",EDGE,"E23.2.0.0")}),1.0]])]});
            var Q3;
            Q3=makeQuery(id+"F19.imprint","IMPRINT",FACE,{"disambiguationData":[TD([[makeQuery(id+"F19.imprint","IMPRINT",EDGE,{"derivedFrom":sQuery(id+"F19.wireOp",EDGE,"E23.3.0.0")}),1.0]])]});
            var Q4;
            Q4=makeQuery(id+"F19.imprint","IMPRINT",FACE,{"disambiguationData":[TD([[makeQuery(id+"F19.imprint","IMPRINT",EDGE,{"derivedFrom":sQuery(id+"F19.wireOp",EDGE,"E23.4.0.0")}),1.0]])]});
            var Q5;
            Q5=makeQuery(id+"F19.imprint","IMPRINT",FACE,{"disambiguationData":[TD([[makeQuery(id+"F19.imprint","IMPRINT",EDGE,{"derivedFrom":sQuery(id+"F19.wireOp",EDGE,"E23.5.0.0")}),1.0]])]});
            var Q6;
            Q6=makeQuery(id+"F19.imprint","IMPRINT",FACE,{"disambiguationData":[TD([[makeQuery(id+"F19.imprint","IMPRINT",EDGE,{"derivedFrom":sQuery(id+"F19.wireOp",EDGE,"E23.6.0.0")}),1.0]])]});
            var Q7;
            Q7=makeQuery(id+"F19.imprint","IMPRINT",FACE,{"disambiguationData":[TD([[makeQuery(id+"F19.imprint","IMPRINT",EDGE,{"derivedFrom":sQuery(id+"F19.wireOp",EDGE,"E23.7.0.0")}),1.0]])]});
            var Q8;
            Q8=makeQuery(id+"F19.imprint","IMPRINT",FACE,{"disambiguationData":[TD([[makeQuery(id+"F19.imprint","IMPRINT",EDGE,{"derivedFrom":sQuery(id+"F19.wireOp",EDGE,"E23.8.0.0")}),1.0]])]});
            var Q9;
            Q9=makeQuery(id+"F19.imprint","IMPRINT",FACE,{"disambiguationData":[TD([[makeQuery(id+"F19.imprint","IMPRINT",EDGE,{"derivedFrom":sQuery(id+"F19.wireOp",EDGE,"E23.9.0.0")}),1.0]])]});
            var Q10;
            Q10=makeQuery(id+"F19.imprint","IMPRINT",FACE,{"disambiguationData":[TD([[makeQuery(id+"F19.imprint","IMPRINT",EDGE,{"derivedFrom":sQuery(id+"F19.wireOp",EDGE,"E23.10.0.0")}),1.0]])]});
            var Q11;
            Q11=makeQuery(id+"F19.imprint","IMPRINT",FACE,{"disambiguationData":[TD([[makeQuery(id+"F19.imprint","IMPRINT",EDGE,{"derivedFrom":sQuery(id+"F19.wireOp",EDGE,"E23.11.0.0")}),1.0]])]});
            var Q12;
            Q12=makeQuery(id+"F19.imprint","IMPRINT",FACE,{"disambiguationData":[TD([[makeQuery(id+"F19.imprint","IMPRINT",EDGE,{"derivedFrom":sQuery(id+"F19.wireOp",EDGE,"E23.12.0.0")}),1.0]])]});
            var Q13;
            Q13=makeQuery(id+"F19.imprint","IMPRINT",FACE,{"disambiguationData":[TD([[makeQuery(id+"F19.imprint","IMPRINT",EDGE,{"derivedFrom":sQuery(id+"F19.wireOp",EDGE,"E23.13.0.0")}),1.0]])]});
            var Q14;
            Q14=makeQuery(id+"F19.imprint","IMPRINT",FACE,{"disambiguationData":[TD([[makeQuery(id+"F19.imprint","IMPRINT",EDGE,{"derivedFrom":sQuery(id+"F19.wireOp",EDGE,"E23.14.0.0")}),1.0]])]});
            var Q15;
            Q15=makeQuery(id+"F19.imprint","IMPRINT",FACE,{"disambiguationData":[TD([[makeQuery(id+"F19.imprint","IMPRINT",EDGE,{"derivedFrom":sQuery(id+"F19.wireOp",EDGE,"E23.15.0.0")}),1.0]])]});
            var Q16;
            Q16=makeQuery(id+"F19.imprint","IMPRINT",FACE,{"disambiguationData":[TD([[makeQuery(id+"F19.imprint","IMPRINT",EDGE,{"derivedFrom":sQuery(id+"F19.wireOp",EDGE,"E23.16.0.0")}),1.0]])]});
            var Q17;
            Q17=makeQuery(id+"F19.imprint","IMPRINT",FACE,{"disambiguationData":[TD([[makeQuery(id+"F19.imprint","IMPRINT",EDGE,{"derivedFrom":sQuery(id+"F19.wireOp",EDGE,"E23.17.0.0")}),1.0]])]});
            var Q18;
            Q18=makeQuery(id+"F19.imprint","IMPRINT",FACE,{"disambiguationData":[TD([[makeQuery(id+"F19.imprint","IMPRINT",EDGE,{"derivedFrom":sQuery(id+"F19.wireOp",EDGE,"E23.18.0.0")}),1.0]])]});
            var Q19;
            Q19=makeQuery(id+"F19.imprint","IMPRINT",FACE,{"disambiguationData":[TD([[makeQuery(id+"F19.imprint","IMPRINT",EDGE,{"derivedFrom":sQuery(id+"F19.wireOp",EDGE,"E23.19.0.0")}),1.0]])]});
            var Q20;
            Q20=makeQuery(id+"F19.imprint","IMPRINT",FACE,{"disambiguationData":[TD([[makeQuery(id+"F19.imprint","IMPRINT",EDGE,{"derivedFrom":sQuery(id+"F19.wireOp",EDGE,"E23.20.0.0")}),1.0]])]});
            var Q21;
            Q21=makeQuery(id+"F19.imprint","IMPRINT",FACE,{"disambiguationData":[TD([[makeQuery(id+"F19.imprint","IMPRINT",EDGE,{"derivedFrom":sQuery(id+"F19.wireOp",EDGE,"E23.21.0.0")}),1.0]])]});
            var Q22;
            Q22=makeQuery(id+"F19.imprint","IMPRINT",FACE,{"disambiguationData":[TD([[makeQuery(id+"F19.imprint","IMPRINT",EDGE,{"derivedFrom":sQuery(id+"F19.wireOp",EDGE,"E23.22.0.0")}),1.0]])]});
            var Q23;
            Q23=makeQuery(id+"F19.imprint","IMPRINT",FACE,{"disambiguationData":[TD([[makeQuery(id+"F19.imprint","IMPRINT",EDGE,{"derivedFrom":sQuery(id+"F19.wireOp",EDGE,"E23.23.0.0")}),1.0]])]});
            var Q24;
            Q24=makeQuery(id+"F19.imprint","IMPRINT",FACE,{"disambiguationData":[TD([[makeQuery(id+"F19.imprint","IMPRINT",EDGE,{"derivedFrom":sQuery(id+"F19.wireOp",EDGE,"E23.24.0.0")}),1.0]])]});
            var Q25;
            Q25=makeQuery(id+"F19.imprint","IMPRINT",FACE,{"disambiguationData":[TD([[makeQuery(id+"F19.imprint","IMPRINT",EDGE,{"derivedFrom":sQuery(id+"F19.wireOp",EDGE,"E23.25.0.0")}),1.0]])]});
            var Q26;
            Q26=makeQuery(id+"F19.imprint","IMPRINT",FACE,{"disambiguationData":[TD([[makeQuery(id+"F19.imprint","IMPRINT",EDGE,{"derivedFrom":sQuery(id+"F19.wireOp",EDGE,"E23.26.0.0")}),1.0]])]});
            var Q27;
            Q27=makeQuery(id+"F19.imprint","IMPRINT",FACE,{"disambiguationData":[TD([[makeQuery(id+"F19.imprint","IMPRINT",EDGE,{"derivedFrom":sQuery(id+"F19.wireOp",EDGE,"E23.27.0.0")}),1.0]])]});
            var Q28;
            Q28=makeQuery(id+"F19.imprint","IMPRINT",FACE,{"disambiguationData":[TD([[makeQuery(id+"F19.imprint","IMPRINT",EDGE,{"derivedFrom":sQuery(id+"F19.wireOp",EDGE,"E23.28.0.0")}),1.0]])]});
            var Q29;
            Q29=makeQuery(id+"F19.imprint","IMPRINT",FACE,{"disambiguationData":[TD([[makeQuery(id+"F19.imprint","IMPRINT",EDGE,{"derivedFrom":sQuery(id+"F19.wireOp",EDGE,"E23.29.0.0")}),1.0]])]});
            var Q30;
            Q30=makeQuery(id+"F19.imprint","IMPRINT",FACE,{"disambiguationData":[TD([[makeQuery(id+"F19.imprint","IMPRINT",EDGE,{"derivedFrom":sQuery(id+"F19.wireOp",EDGE,"E23.30.0.0")}),1.0]])]});
            var Q31;
            Q31=makeQuery(id+"F19.imprint","IMPRINT",FACE,{"disambiguationData":[TD([[makeQuery(id+"F19.imprint","IMPRINT",EDGE,{"derivedFrom":sQuery(id+"F19.wireOp",EDGE,"E23.31.0.0")}),1.0]])]});
            var Q32;
            Q32=makeQuery(id+"F19.imprint","IMPRINT",FACE,{"disambiguationData":[TD([[makeQuery(id+"F19.imprint","IMPRINT",EDGE,{"derivedFrom":sQuery(id+"F19.wireOp",EDGE,"E23.32.0.0")}),1.0]])]});
            var Q33;
            Q33=makeQuery(id+"F19.imprint","IMPRINT",FACE,{"disambiguationData":[TD([[makeQuery(id+"F19.imprint","IMPRINT",EDGE,{"derivedFrom":sQuery(id+"F19.wireOp",EDGE,"E23.33.0.0")}),1.0]])]});
            var Q34;
            Q34=makeQuery(id+"F19.imprint","IMPRINT",FACE,{"disambiguationData":[TD([[makeQuery(id+"F19.imprint","IMPRINT",EDGE,{"derivedFrom":sQuery(id+"F19.wireOp",EDGE,"E23.34.0.0")}),1.0]])]});
            var Q35;
            Q35=makeQuery(id+"F19.imprint","IMPRINT",FACE,{"disambiguationData":[TD([[makeQuery(id+"F19.imprint","IMPRINT",EDGE,{"derivedFrom":sQuery(id+"F19.wireOp",EDGE,"E23.35.0.0")}),1.0]])]});
            var Q36;
            Q36=makeQuery(id+"F19.imprint","IMPRINT",FACE,{"disambiguationData":[TD([[makeQuery(id+"F19.imprint","IMPRINT",EDGE,{"derivedFrom":sQuery(id+"F19.wireOp",EDGE,"E23.36.0.0")}),1.0]])]});
            var Q37;
            Q37=makeQuery(id+"F19.imprint","IMPRINT",FACE,{"disambiguationData":[TD([[makeQuery(id+"F19.imprint","IMPRINT",EDGE,{"derivedFrom":sQuery(id+"F19.wireOp",EDGE,"E23.37.0.0")}),1.0]])]});
            var Q38;
            Q38=makeQuery(id+"F19.imprint","IMPRINT",FACE,{"disambiguationData":[TD([[makeQuery(id+"F19.imprint","IMPRINT",EDGE,{"derivedFrom":sQuery(id+"F19.wireOp",EDGE,"E23.38.0.0")}),1.0]])]});
            var Q39;
            Q39=makeQuery(id+"F19.imprint","IMPRINT",FACE,{"disambiguationData":[TD([[makeQuery(id+"F19.imprint","IMPRINT",EDGE,{"derivedFrom":sQuery(id+"F19.wireOp",EDGE,"E23.39.0.0")}),1.0]])]});
            var Q40;
            Q40=makeQuery(id+"F19.imprint","IMPRINT",FACE,{"disambiguationData":[TD([[makeQuery(id+"F19.imprint","IMPRINT",EDGE,{"derivedFrom":sQuery(id+"F19.wireOp",EDGE,"E23.40.0.0")}),1.0]])]});
            var Q41;
            Q41=makeQuery(id+"F19.imprint","IMPRINT",FACE,{"disambiguationData":[TD([[makeQuery(id+"F19.imprint","IMPRINT",EDGE,{"derivedFrom":sQuery(id+"F19.wireOp",EDGE,"E23.41.0.0")}),1.0]])]});
            var Q42;
            Q42=makeQuery(id+"F19.imprint","IMPRINT",FACE,{"disambiguationData":[TD([[makeQuery(id+"F19.imprint","IMPRINT",EDGE,{"derivedFrom":sQuery(id+"F19.wireOp",EDGE,"E23.42.0.0")}),1.0]])]});
            var Q43;
            Q43=makeQuery(id+"F19.imprint","IMPRINT",FACE,{"disambiguationData":[TD([[makeQuery(id+"F19.imprint","IMPRINT",EDGE,{"derivedFrom":sQuery(id+"F19.wireOp",EDGE,"E23.43.0.0")}),1.0]])]});
            var Q44;
            Q44=makeQuery(id+"F19.imprint","IMPRINT",FACE,{"disambiguationData":[TD([[makeQuery(id+"F19.imprint","IMPRINT",EDGE,{"derivedFrom":sQuery(id+"F19.wireOp",EDGE,"E23.44.0.0")}),1.0]])]});
            var Q45;
            Q45=makeQuery(id+"F19.imprint","IMPRINT",FACE,{"disambiguationData":[TD([[makeQuery(id+"F19.imprint","IMPRINT",EDGE,{"derivedFrom":sQuery(id+"F19.wireOp",EDGE,"E23.45.0.0")}),1.0]])]});
            var Q46;
            Q46=makeQuery(id+"F19.imprint","IMPRINT",FACE,{"disambiguationData":[TD([[makeQuery(id+"F19.imprint","IMPRINT",EDGE,{"derivedFrom":sQuery(id+"F19.wireOp",EDGE,"E23.46.0.0")}),1.0]])]});
            var Q47;
            Q47=makeQuery(id+"F19.imprint","IMPRINT",FACE,{"disambiguationData":[TD([[makeQuery(id+"F19.imprint","IMPRINT",EDGE,{"derivedFrom":sQuery(id+"F19.wireOp",EDGE,"E23.47.0.0")}),1.0]])]});
            var Q48;
            Q48=makeQuery(id+"F19.imprint","IMPRINT",FACE,{"disambiguationData":[TD([[makeQuery(id+"F19.imprint","IMPRINT",EDGE,{"derivedFrom":sQuery(id+"F19.wireOp",EDGE,"E23.48.0.0")}),1.0]])]});
            var Q49;
            Q49=makeQuery(id+"F19.imprint","IMPRINT",FACE,{"disambiguationData":[TD([[makeQuery(id+"F19.imprint","IMPRINT",EDGE,{"derivedFrom":sQuery(id+"F19.wireOp",EDGE,"E23.49.0.0")}),1.0]])]});
            extrude(context, id + "F20", {"entities" : qUnion([Q0, Q1, Q2, Q3, Q4, Q5, Q6, Q7, Q8, Q9, Q10, Q11, Q12, Q13, Q14, Q15, Q16, Q17, Q18, Q19, Q20, Q21, Q22, Q23, Q24, Q25, Q26, Q27, Q28, Q29, Q30, Q31, Q32, Q33, Q34, Q35, Q36, Q37, Q38, Q39, Q40, Q41, Q42, Q43, Q44, Q45, Q46, Q47, Q48, Q49]), "operationType" : NewBodyOperationType.REMOVE, "oppositeDirection" : true, "depth" : 0.25 * mm, "offsetDistance" : 25.4 * mm});
        }
        {
            var Q0;
            Q0=makeQuery(id+"F1.opExtrude","SWEPT_FACE",FACE,{"disambiguationData":[OSD([sQuery(id+"F0.wireOp",EDGE,"E3")])]});
            var sketch = newSketch(context, id + "F21", { "sketchPlane" : qUnion([Q0])});
            skLineSegment(sketch, "E24.bottom", {"start": v(-1.88, -8.9) * mm, "end": v(-3.7, -8.9) * mm});
            skLineSegment(sketch, "E24.top", {"start": v(-1.88, 4.1) * mm, "end": v(-3.7, 4.1) * mm});
            skLineSegment(sketch, "E24.left", {"start": v(-1.88, -8.9) * mm, "end": v(-1.88, 4.1) * mm});
            skLineSegment(sketch, "E24.right", {"start": v(-3.7, -8.9) * mm, "end": v(-3.7, 4.1) * mm});
            skSolve(sketch);
        }
        {
            var Q0;
            Q0=makeQuery(id+"F21.imprint","IMPRINT",FACE,{"disambiguationData":[TD([[makeQuery(id+"F21.imprint","IMPRINT",EDGE,{"derivedFrom":sQuery(id+"F21.wireOp",EDGE,"E24.bottom")}),-1.0]])]});
            extrude(context, id + "F22", {"entities" : qUnion([Q0]), "operationType" : NewBodyOperationType.REMOVE, "oppositeDirection" : true, "depth" : 0.25 * mm, "offsetDistance" : 25.4 * mm});
        }
        {
            var Q0;
            Q0=makeQuery(id+"F22.boolean.opBoolean","COPY",FACE,{"derivedFrom":makeQuery(id+"F22.opExtrude","CAP_FACE",FACE,{"disambiguationData":[OSD([sQuery(id+"F21.wireOp",EDGE,"E24.bottom"),sQuery(id+"F21.wireOp",EDGE,"E24.top"),sQuery(id+"F21.wireOp",EDGE,"E24.left"),sQuery(id+"F21.wireOp",EDGE,"E24.right")])],"isStart":false})});
            var sketch = newSketch(context, id + "F23", { "sketchPlane" : qUnion([Q0])});
            skLineSegment(sketch, "E25", {"start": v(-2.79, -8.9) * mm, "end": v(-2.79, 4.1) * mm, "construction": true});
            skCircle(sketch, "E26", {"center": v(-2.79, -7.32) * mm, "radius": 0.6 * mm});
            skCircle(sketch, "E27.1.0.0", {"center": v(-2.78, -5.67) * mm, "radius": 0.6 * mm});
            skCircle(sketch, "E27.2.0.0", {"center": v(-2.78, -4.02) * mm, "radius": 0.6 * mm});
            skCircle(sketch, "E27.3.0.0", {"center": v(-2.78, -2.37) * mm, "radius": 0.6 * mm});
            skCircle(sketch, "E27.4.0.0", {"center": v(-2.78, -0.72) * mm, "radius": 0.6 * mm});
            skCircle(sketch, "E27.5.0.0", {"center": v(-2.77, 0.93) * mm, "radius": 0.6 * mm});
            skCircle(sketch, "E27.6.0.0", {"center": v(-2.77, 2.59) * mm, "radius": 0.6 * mm});
            skLineSegment(sketch, "E27.direction1", {"start": v(-2.79, -7.32) * mm, "end": v(-2.78, -5.67) * mm, "construction": true});
            skSolve(sketch);
        }
        {
            var Q0;
            Q0=makeQuery(id+"F23.imprint","IMPRINT",FACE,{"disambiguationData":[TD([[makeQuery(id+"F23.imprint","IMPRINT",EDGE,{"derivedFrom":sQuery(id+"F23.wireOp",EDGE,"E26")}),1.0]])]});
            var Q1;
            Q1=makeQuery(id+"F23.imprint","IMPRINT",FACE,{"disambiguationData":[TD([[makeQuery(id+"F23.imprint","IMPRINT",EDGE,{"derivedFrom":sQuery(id+"F23.wireOp",EDGE,"E27.1.0.0")}),1.0]])]});
            var Q2;
            Q2=makeQuery(id+"F23.imprint","IMPRINT",FACE,{"disambiguationData":[TD([[makeQuery(id+"F23.imprint","IMPRINT",EDGE,{"derivedFrom":sQuery(id+"F23.wireOp",EDGE,"E27.2.0.0")}),1.0]])]});
            var Q3;
            Q3=makeQuery(id+"F23.imprint","IMPRINT",FACE,{"disambiguationData":[TD([[makeQuery(id+"F23.imprint","IMPRINT",EDGE,{"derivedFrom":sQuery(id+"F23.wireOp",EDGE,"E27.3.0.0")}),1.0]])]});
            var Q4;
            Q4=makeQuery(id+"F23.imprint","IMPRINT",FACE,{"disambiguationData":[TD([[makeQuery(id+"F23.imprint","IMPRINT",EDGE,{"derivedFrom":sQuery(id+"F23.wireOp",EDGE,"E27.4.0.0")}),1.0]])]});
            var Q5;
            Q5=makeQuery(id+"F23.imprint","IMPRINT",FACE,{"disambiguationData":[TD([[makeQuery(id+"F23.imprint","IMPRINT",EDGE,{"derivedFrom":sQuery(id+"F23.wireOp",EDGE,"E27.5.0.0")}),1.0]])]});
            var Q6;
            Q6=makeQuery(id+"F23.imprint","IMPRINT",FACE,{"disambiguationData":[TD([[makeQuery(id+"F23.imprint","IMPRINT",EDGE,{"derivedFrom":sQuery(id+"F23.wireOp",EDGE,"E27.6.0.0")}),1.0]])]});
            extrude(context, id + "F24", {"entities" : qUnion([Q0, Q1, Q2, Q3, Q4, Q5, Q6]), "depth" : 0.38 * mm, "offsetDistance" : 25.4 * mm});
        }
        {
            var Q0;
            Q0=makeQuery(id+"F22.boolean.opBoolean","COPY",EDGE,{"derivedFrom":makeQuery(id+"F22.opExtrude","SWEPT_EDGE",EDGE,{"disambiguationData":[OSD([sQuery(id+"F21.wireOp",EDGE,"E24.top"),sQuery(id+"F21.wireOp",EDGE,"E24.right")])]})});
            var Q1;
            Q1=makeQuery(id+"F22.boolean.opBoolean","COPY",EDGE,{"derivedFrom":makeQuery(id+"F22.opExtrude","SWEPT_EDGE",EDGE,{"disambiguationData":[OSD([sQuery(id+"F21.wireOp",EDGE,"E24.top"),sQuery(id+"F21.wireOp",EDGE,"E24.left")])]})});
            var Q2;
            Q2=makeQuery(id+"F22.boolean.opBoolean","COPY",EDGE,{"derivedFrom":makeQuery(id+"F22.opExtrude","SWEPT_EDGE",EDGE,{"disambiguationData":[OSD([sQuery(id+"F21.wireOp",EDGE,"E24.bottom"),sQuery(id+"F21.wireOp",EDGE,"E24.left")])]})});
            var Q3;
            Q3=makeQuery(id+"F22.boolean.opBoolean","COPY",EDGE,{"derivedFrom":makeQuery(id+"F22.opExtrude","SWEPT_EDGE",EDGE,{"disambiguationData":[OSD([sQuery(id+"F21.wireOp",EDGE,"E24.bottom"),sQuery(id+"F21.wireOp",EDGE,"E24.right")])]})});
            fillet(context, id + "F25", {"entities" : qUnion([Q0, Q1, Q2, Q3]), "radius" : 0.25 * mm, "tangentPropagation" : true, "allowEdgeOverflow" : false});
        }
        {
            var Q0;
            Q0=makeQuery(id+"F1.opExtrude","CAP_FACE",FACE,{"disambiguationData":[OSD([sQuery(id+"F0.wireOp",EDGE,"E0"),sQuery(id+"F0.wireOp",EDGE,"E1"),sQuery(id+"F0.wireOp",EDGE,"E2"),sQuery(id+"F0.wireOp",EDGE,"E3")])],"isStart":false});
            var sketch = newSketch(context, id + "F26", { "sketchPlane" : qUnion([Q0])});
            skLineSegment(sketch, "E28.bottom", {"start": v(13.2, 13.82) * mm, "end": v(20.97, 13.82) * mm});
            skLineSegment(sketch, "E28.top", {"start": v(13.2, 10) * mm, "end": v(20.97, 10) * mm});
            skLineSegment(sketch, "E28.left", {"start": v(13.2, 13.82) * mm, "end": v(13.2, 10) * mm});
            skLineSegment(sketch, "E28.right", {"start": v(20.97, 13.82) * mm, "end": v(20.97, 10) * mm});
            skSolve(sketch);
        }
        {
            var Q0;
            Q0=makeQuery(id+"F26.imprint","IMPRINT",FACE,{"disambiguationData":[TD([[makeQuery(id+"F26.imprint","IMPRINT",EDGE,{"derivedFrom":sQuery(id+"F26.wireOp",EDGE,"E28.bottom")}),-1.0]])]});
            extrude(context, id + "F27", {"entities" : qUnion([Q0]), "operationType" : NewBodyOperationType.REMOVE, "oppositeDirection" : true, "depth" : 1.27 * mm, "offsetDistance" : 25.4 * mm});
        }
        {
            var Q0;
            Q0=makeQuery(id+"F27.boolean.opBoolean","COPY",FACE,{"derivedFrom":makeQuery(id+"F27.opExtrude","CAP_FACE",FACE,{"disambiguationData":[OSD([sQuery(id+"F26.wireOp",EDGE,"E28.bottom"),sQuery(id+"F26.wireOp",EDGE,"E28.top"),sQuery(id+"F26.wireOp",EDGE,"E28.left"),sQuery(id+"F26.wireOp",EDGE,"E28.right")])],"isStart":false})});
            extrude(context, id + "F28", {"entities" : qUnion([Q0]), "depth" : 0.03 * mm, "offsetDistance" : 25.4 * mm});
        }
        {
            var Q0;
            Q0=makeQuery(id+"F27.boolean.opBoolean","COPY",EDGE,{"derivedFrom":makeQuery(id+"F27.opExtrude","SWEPT_EDGE",EDGE,{"disambiguationData":[OSD([sQuery(id+"F26.wireOp",EDGE,"E28.bottom"),sQuery(id+"F26.wireOp",EDGE,"E28.left")])]})});
            var Q1;
            Q1=makeQuery(id+"F27.boolean.opBoolean","COPY",EDGE,{"derivedFrom":makeQuery(id+"F27.opExtrude","SWEPT_EDGE",EDGE,{"disambiguationData":[OSD([sQuery(id+"F26.wireOp",EDGE,"E28.top"),sQuery(id+"F26.wireOp",EDGE,"E28.left")])]})});
            var Q2;
            Q2=makeQuery(id+"F27.boolean.opBoolean","COPY",EDGE,{"derivedFrom":makeQuery(id+"F27.opExtrude","SWEPT_EDGE",EDGE,{"disambiguationData":[OSD([sQuery(id+"F26.wireOp",EDGE,"E28.top"),sQuery(id+"F26.wireOp",EDGE,"E28.right")])]})});
            var Q3;
            Q3=makeQuery(id+"F27.boolean.opBoolean","COPY",EDGE,{"derivedFrom":makeQuery(id+"F27.opExtrude","SWEPT_EDGE",EDGE,{"disambiguationData":[OSD([sQuery(id+"F26.wireOp",EDGE,"E28.bottom"),sQuery(id+"F26.wireOp",EDGE,"E28.right")])]})});
            fillet(context, id + "F29", {"entities" : qUnion([Q0, Q1, Q2, Q3]), "radius" : 0.92 * mm, "tangentPropagation" : true, "allowEdgeOverflow" : false});
        }
        {
            var Q0;
            Q0=makeQuery(id+"F28.opExtrude","CAP_FACE",FACE,{"disambiguationData":[OSD([sQuery(id+"F26.wireOp",EDGE,"E28.bottom"),sQuery(id+"F26.wireOp",EDGE,"E28.top"),sQuery(id+"F26.wireOp",EDGE,"E28.left"),sQuery(id+"F26.wireOp",EDGE,"E28.right")])],"isStart":false});
            var sketch = newSketch(context, id + "F30", { "sketchPlane" : qUnion([Q0])});
            skCircle(sketch, "E29", {"center": v(15.1, 11.9) * mm, "radius": 0.7 * mm});
            skCircle(sketch, "E30", {"center": v(15.1, 11.9) * mm, "radius": 0.4 * mm});
            skCircle(sketch, "E31.1.0.0", {"center": v(16.97, 11.9) * mm, "radius": 0.4 * mm});
            skCircle(sketch, "E31.1.0.1", {"center": v(16.97, 11.9) * mm, "radius": 0.7 * mm});
            skCircle(sketch, "E31.2.0.0", {"center": v(18.85, 11.9) * mm, "radius": 0.4 * mm});
            skCircle(sketch, "E31.2.0.1", {"center": v(18.85, 11.9) * mm, "radius": 0.7 * mm});
            skLineSegment(sketch, "E31.direction1", {"start": v(15.1, 11.9) * mm, "end": v(16.97, 11.9) * mm, "construction": true});
            skSolve(sketch);
        }
        {
            var Q0;
            Q0=makeQuery(id+"F30.imprint","IMPRINT",FACE,{"disambiguationData":[TD([[makeQuery(id+"F30.imprint","IMPRINT",EDGE,{"derivedFrom":sQuery(id+"F30.wireOp",EDGE,"E29")}),1.0]])]});
            var Q1;
            Q1=makeQuery(id+"F30.imprint","IMPRINT",FACE,{"disambiguationData":[TD([[makeQuery(id+"F30.imprint","IMPRINT",EDGE,{"derivedFrom":sQuery(id+"F30.wireOp",EDGE,"E31.1.0.0")}),-1.0]])]});
            var Q2;
            Q2=makeQuery(id+"F30.imprint","IMPRINT",FACE,{"disambiguationData":[TD([[makeQuery(id+"F30.imprint","IMPRINT",EDGE,{"derivedFrom":sQuery(id+"F30.wireOp",EDGE,"E31.2.0.0")}),-1.0]])]});
            extrude(context, id + "F31", {"entities" : qUnion([Q0, Q1, Q2]), "depth" : 0.76 * mm, "offsetDistance" : 25.4 * mm});
        }
    });
